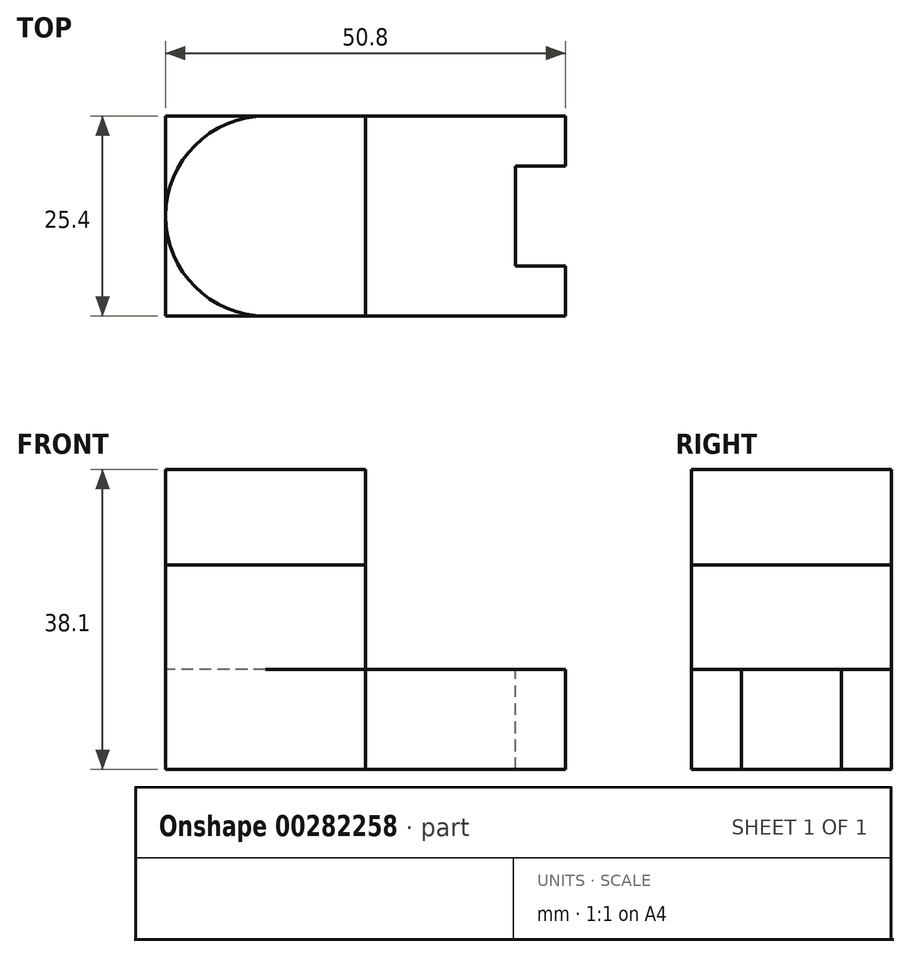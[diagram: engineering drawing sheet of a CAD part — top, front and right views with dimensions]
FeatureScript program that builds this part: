
annotation { "Feature Type Name" : "Feature", "Feature Type Description" : "" }
export const myFeature = defineFeature(function(context is Context, id is Id, definition is map)
    precondition{}
    {
        {
            var Q0;
            Q0=qCreatedBy(makeId("Right.planeOp"),FACE);
            var sketch = newSketch(context, id + "F0", { "sketchPlane" : qUnion([Q0])});
            skLineSegment(sketch, "E0", {"start": v(0, 0) * mm, "end": v(6.35, 0) * mm});
            skLineSegment(sketch, "E1", {"start": v(6.35, 0) * mm, "end": v(6.35, 12.7) * mm});
            skLineSegment(sketch, "E2", {"start": v(6.35, 12.7) * mm, "end": v(0, 12.7) * mm});
            skLineSegment(sketch, "E3", {"start": v(0, 12.7) * mm, "end": v(0, 0) * mm});
            skLineSegment(sketch, "E4", {"start": v(6.35, 12.7) * mm, "end": v(19.05, 12.7) * mm});
            skLineSegment(sketch, "E5", {"start": v(19.05, 12.7) * mm, "end": v(19.05, 0) * mm});
            skLineSegment(sketch, "E6", {"start": v(19.05, 0) * mm, "end": v(6.35, 0) * mm});
            skLineSegment(sketch, "E7", {"start": v(19.05, 12.7) * mm, "end": v(25.4, 12.7) * mm});
            skLineSegment(sketch, "E8", {"start": v(25.4, 12.7) * mm, "end": v(25.4, 0) * mm});
            skLineSegment(sketch, "E9", {"start": v(25.4, 0) * mm, "end": v(19.05, 0) * mm});
            skSolve(sketch);
        }
        {
            var Q0;
            Q0 = qSketchRegion(id + "F0", true);
            extrude(context, id + "F1", {"entities" : qUnion([Q0]), "depth" : 25.4 * mm});
        }
        {
            var Q0;
            Q0=makeQuery(id+"F1.opExtrude","SWEPT_FACE",FACE,{"disambiguationData":[OSD([sQuery(id+"F0.wireOp",EDGE,"E2"),sQuery(id+"F0.wireOp",EDGE,"E4"),sQuery(id+"F0.wireOp",EDGE,"E7")])]});
            var sketch = newSketch(context, id + "F2", { "sketchPlane" : qUnion([Q0])});
            skLineSegment(sketch, "E10", {"start": v(25.4, 0) * mm, "end": v(25.4, 6.35) * mm});
            skLineSegment(sketch, "E11", {"start": v(25.4, 6.35) * mm, "end": v(19.05, 6.35) * mm});
            skLineSegment(sketch, "E12", {"start": v(19.05, 6.35) * mm, "end": v(19.05, 19.05) * mm});
            skLineSegment(sketch, "E13", {"start": v(19.05, 19.05) * mm, "end": v(25.4, 19.05) * mm});
            skLineSegment(sketch, "E14", {"start": v(25.4, 19.05) * mm, "end": v(25.4, 25.4) * mm});
            skSolve(sketch);
        }
        {
            var Q0;
            {var subQ0=sQuery(id+"F2.wireOp",EDGE,"E11");Q0=makeQuery(id+"F2.imprint","IMPRINT",FACE,{"disambiguationData":[TD([[makeQuery(id+"F2.imprint","IMPRINT",EDGE,{"derivedFrom":subQ0}),-1.0]])]});}
            extrude(context, id + "F3", {"entities" : qUnion([Q0]), "operationType" : NewBodyOperationType.REMOVE, "endBound" : BoundingType.THROUGH_ALL, "oppositeDirection" : true, "depth" : 25.4 * mm});
        }
        {
            var Q0;
            Q0=makeQuery(id+"F1.opExtrude","SWEPT_FACE",FACE,{"disambiguationData":[OSD([sQuery(id+"F0.wireOp",EDGE,"E2"),sQuery(id+"F0.wireOp",EDGE,"E4"),sQuery(id+"F0.wireOp",EDGE,"E7")])]});
            var sketch = newSketch(context, id + "F4", { "sketchPlane" : qUnion([Q0])});
            skLineSegment(sketch, "E15", {"start": v(0, 0) * mm, "end": v(-12.7, 0) * mm});
            skLineSegment(sketch, "E16", {"start": v(0, 25.4) * mm, "end": v(-12.7, 25.4) * mm});
            skArc(sketch, "E17", {"start": v(-12.7, 0) * mm, "mid": v(-25.4, 12.7) * mm, "end": v(-12.7, 25.4) * mm});
            skSolve(sketch);
        }
        {
            var Q0;
            Q0=makeQuery(id+"F4.imprint","IMPRINT",FACE,{"disambiguationData":[TD([[makeQuery(id+"F4.imprint","IMPRINT",EDGE,{"derivedFrom":sQuery(id+"F4.wireOp",EDGE,"E15")}),-1.0]])]});
            extrude(context, id + "F5", {"entities" : qUnion([Q0]), "depth" : 25.4 * mm});
        }
        {
            var Q0;
            Q0=makeQuery(id+"F1.opExtrude","CAP_FACE",FACE,{"disambiguationData":[OSD([sQuery(id+"F0.wireOp",EDGE,"E0"),sQuery(id+"F0.wireOp",EDGE,"E2"),sQuery(id+"F0.wireOp",EDGE,"E3"),sQuery(id+"F0.wireOp",EDGE,"E4"),sQuery(id+"F0.wireOp",EDGE,"E6"),sQuery(id+"F0.wireOp",EDGE,"E7"),sQuery(id+"F0.wireOp",EDGE,"E8"),sQuery(id+"F0.wireOp",EDGE,"E9")])],"isStart":true});
            var sketch = newSketch(context, id + "F6", { "sketchPlane" : qUnion([Q0])});
            skLineSegment(sketch, "E18", {"start": v(-25.4, 0) * mm, "end": v(-25.4, 25.97) * mm});
            skLineSegment(sketch, "E19", {"start": v(-25.4, 25.97) * mm, "end": v(0, 25.97) * mm});
            skLineSegment(sketch, "E20", {"start": v(0, 25.97) * mm, "end": v(0, 0) * mm});
            skLineSegment(sketch, "E21", {"start": v(0, 0) * mm, "end": v(-25.4, 0) * mm});
            skSolve(sketch);
        }
        {
            var Q0;
            Q0 = qSketchRegion(id + "F6", true);
            extrude(context, id + "F7", {"entities" : qUnion([Q0]), "depth" : 25.4 * mm});
        }
    });
